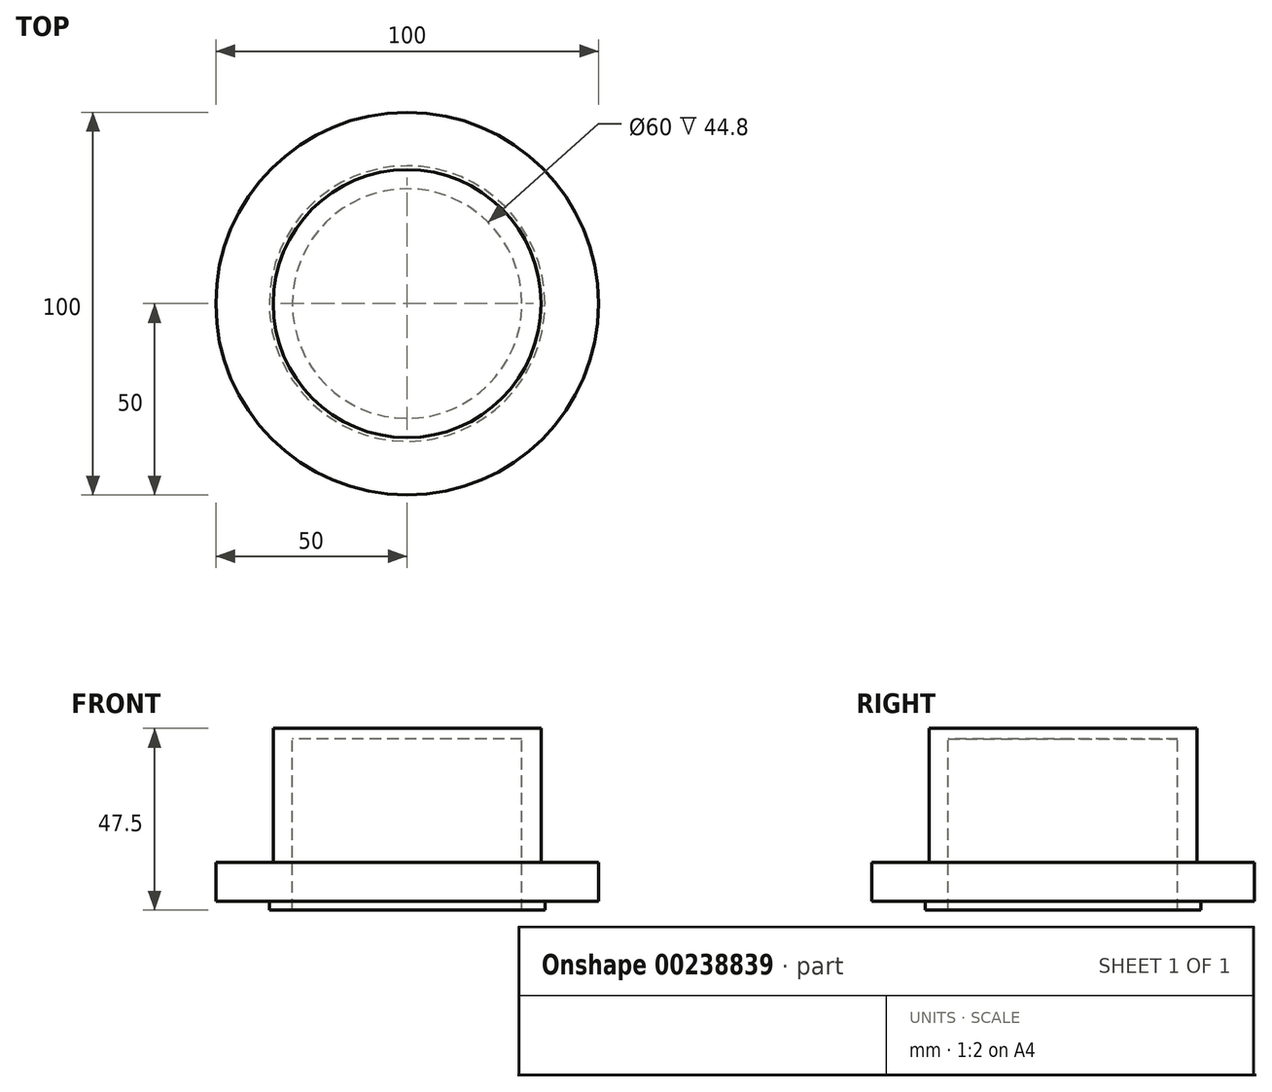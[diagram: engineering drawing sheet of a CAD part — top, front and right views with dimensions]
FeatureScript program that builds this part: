
annotation { "Feature Type Name" : "Feature", "Feature Type Description" : "" }
export const myFeature = defineFeature(function(context is Context, id is Id, definition is map)
    precondition{}
    {
        {
            var Q0;
            Q0=qCreatedBy(makeId("Front.planeOp"),FACE);
            var sketch = newSketch(context, id + "F0", { "sketchPlane" : qUnion([Q0])});
            skLineSegment(sketch, "E0", {"start": v(0, 60.15) * mm, "end": v(0, -70.3) * mm, "construction": true});
            skLineSegment(sketch, "E1", {"start": v(0, 36.75) * mm, "end": v(35, 36.75) * mm});
            skLineSegment(sketch, "E2", {"start": v(35, 36.75) * mm, "end": v(35, 1.75) * mm});
            skLineSegment(sketch, "E3", {"start": v(35, 1.75) * mm, "end": v(50, 1.75) * mm});
            skLineSegment(sketch, "E4", {"start": v(50, 1.75) * mm, "end": v(50, -8.45) * mm});
            skLineSegment(sketch, "E5", {"start": v(36, -10.75) * mm, "end": v(30, -10.75) * mm});
            skLineSegment(sketch, "E6", {"start": v(30, -10.75) * mm, "end": v(30, 34.05) * mm});
            skLineSegment(sketch, "E7", {"start": v(30, 34.05) * mm, "end": v(0, 34.05) * mm});
            skLineSegment(sketch, "E8", {"start": v(0, 34.05) * mm, "end": v(0, 36.75) * mm});
            skLineSegment(sketch, "E9", {"start": v(36, -10.75) * mm, "end": v(36, -8.45) * mm});
            skLineSegment(sketch, "E10", {"start": v(36, -8.45) * mm, "end": v(50, -8.45) * mm});
            skSolve(sketch);
        }
        {
            var Q0;
            Q0=makeQuery(id+"F0.imprint","IMPRINT",FACE,{"disambiguationData":[TD([[makeQuery(id+"F0.imprint","IMPRINT",EDGE,{"derivedFrom":sQuery(id+"F0.wireOp",EDGE,"E1")}),-1.0]])]});
            var Q1;
            Q1=sQuery(id+"F0.wireOp",EDGE,"E0");
            revolve(context, id + "F1", {"entities" : qUnion([Q0]), "axis" : qUnion([Q1]), "revolveType" : RevolveType.FULL});
        }
    });
